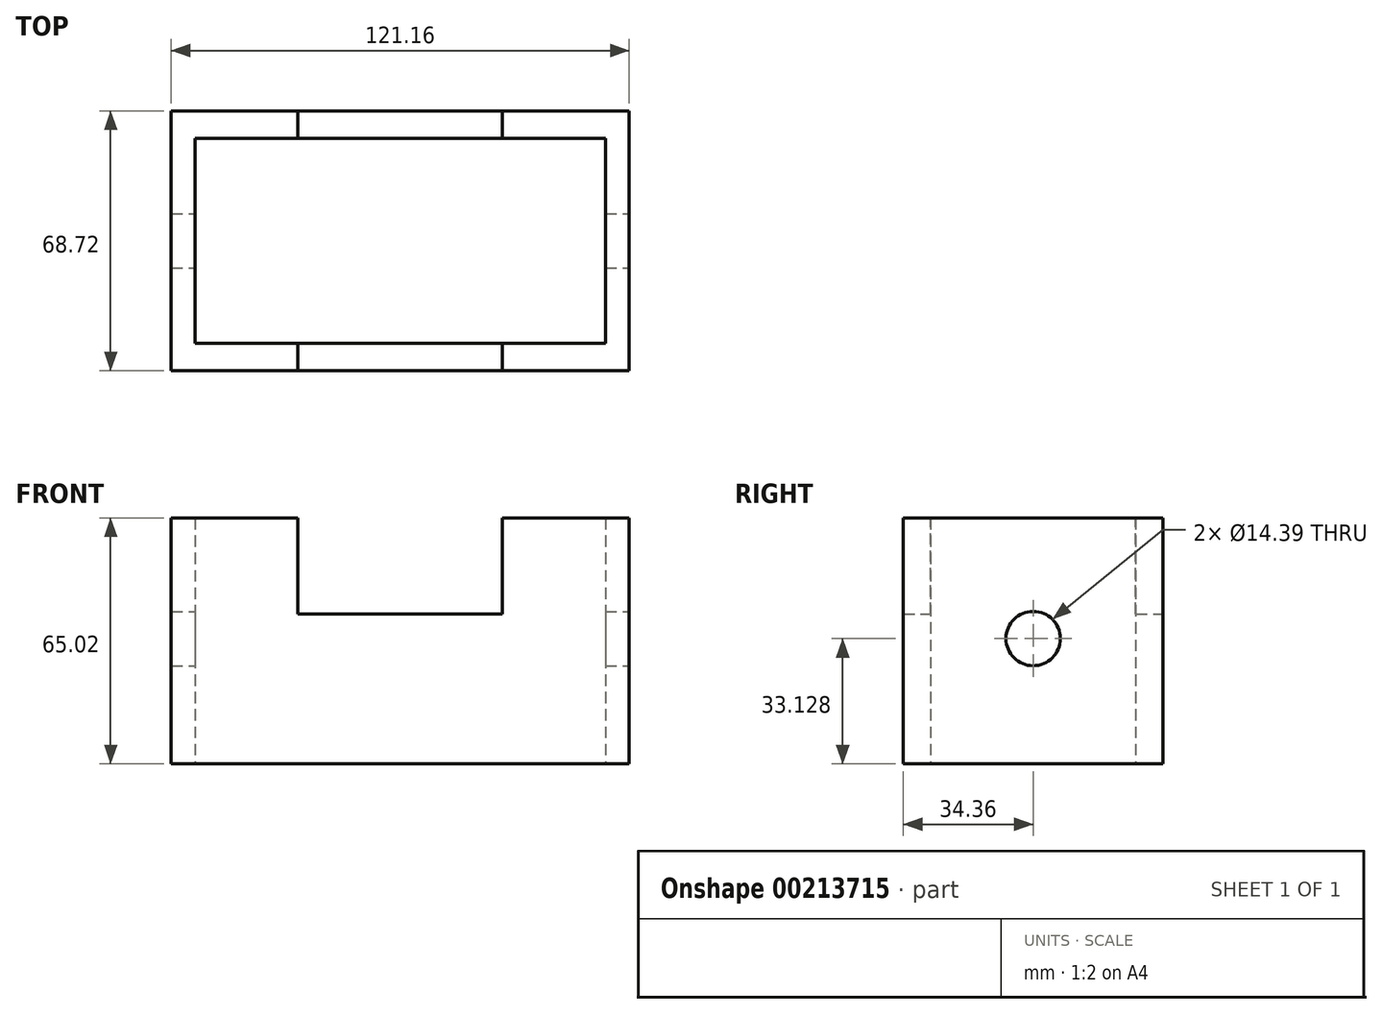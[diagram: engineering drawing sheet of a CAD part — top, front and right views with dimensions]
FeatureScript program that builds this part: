
annotation { "Feature Type Name" : "Feature", "Feature Type Description" : "" }
export const myFeature = defineFeature(function(context is Context, id is Id, definition is map)
    precondition{}
    {
        {
            var Q0;
            Q0=qCreatedBy(makeId("Top.planeOp"),FACE);
            var sketch = newSketch(context, id + "F0", { "sketchPlane" : qUnion([Q0])});
            skLineSegment(sketch, "E0.bottom", {"start": v(60.58, -34.36) * mm, "end": v(-60.58, -34.36) * mm});
            skLineSegment(sketch, "E0.top", {"start": v(60.58, 34.36) * mm, "end": v(-60.58, 34.36) * mm});
            skLineSegment(sketch, "E0.left", {"start": v(60.58, -34.36) * mm, "end": v(60.58, 34.36) * mm});
            skLineSegment(sketch, "E0.right", {"start": v(-60.58, -34.36) * mm, "end": v(-60.58, 34.36) * mm});
            skPoint(sketch, "E0.middle", {"position": v(0, 0) * mm});
            skLineSegment(sketch, "E1.bottom", {"start": v(54.26, -27.13) * mm, "end": v(-54.26, -27.13) * mm});
            skLineSegment(sketch, "E1.top", {"start": v(54.26, 27.13) * mm, "end": v(-54.26, 27.13) * mm});
            skLineSegment(sketch, "E1.left", {"start": v(54.26, -27.13) * mm, "end": v(54.26, 27.13) * mm});
            skLineSegment(sketch, "E1.right", {"start": v(-54.26, -27.13) * mm, "end": v(-54.26, 27.13) * mm});
            skSolve(sketch);
        }
        {
            var Q0;
            Q0 = qSketchRegion(id + "F0", true);
            extrude(context, id + "F1", {"entities" : qUnion([Q0]), "depth" : 65.02 * mm});
        }
        {
            var Q0;
            Q0=makeQuery(id+"F1.opExtrude","CAP_FACE",FACE,{"disambiguationData":[OSD([sQuery(id+"F0.wireOp",EDGE,"E0.bottom"),sQuery(id+"F0.wireOp",EDGE,"E0.top"),sQuery(id+"F0.wireOp",EDGE,"E0.left"),sQuery(id+"F0.wireOp",EDGE,"E0.right"),sQuery(id+"F0.wireOp",EDGE,"E1.bottom"),sQuery(id+"F0.wireOp",EDGE,"E1.top"),sQuery(id+"F0.wireOp",EDGE,"E1.left"),sQuery(id+"F0.wireOp",EDGE,"E1.right")])],"isStart":false});
            var sketch = newSketch(context, id + "F2", { "sketchPlane" : qUnion([Q0])});
            skLineSegment(sketch, "E2.bottom", {"start": v(27.05, -59.7) * mm, "end": v(-27.05, -59.7) * mm});
            skLineSegment(sketch, "E2.top", {"start": v(27.05, 59.7) * mm, "end": v(-27.05, 59.7) * mm});
            skLineSegment(sketch, "E2.left", {"start": v(27.05, -59.7) * mm, "end": v(27.05, 59.7) * mm});
            skLineSegment(sketch, "E2.right", {"start": v(-27.05, -59.7) * mm, "end": v(-27.05, 59.7) * mm});
            skPoint(sketch, "E2.middle", {"position": v(0, 0) * mm});
            skSolve(sketch);
        }
        {
            var Q0;
            Q0 = qSketchRegion(id + "F2", true);
            extrude(context, id + "F3", {"entities" : qUnion([Q0]), "operationType" : NewBodyOperationType.REMOVE, "oppositeDirection" : true, "depth" : 25.4 * mm});
        }
        {
            var Q0;
            Q0=makeQuery(id+"F1.opExtrude","SWEPT_FACE",FACE,{"disambiguationData":[OSD([sQuery(id+"F0.wireOp",EDGE,"E0.left")])]});
            var sketch = newSketch(context, id + "F4", { "sketchPlane" : qUnion([Q0])});
            skCircle(sketch, "E3", {"center": v(0, 33.13) * mm, "radius": 7.2 * mm});
            skSolve(sketch);
        }
        {
            var Q0;
            Q0 = qSketchRegion(id + "F4", true);
            extrude(context, id + "F5", {"entities" : qUnion([Q0]), "operationType" : NewBodyOperationType.REMOVE, "endBound" : BoundingType.THROUGH_ALL, "oppositeDirection" : true, "depth" : 25.4 * mm});
        }
    });
